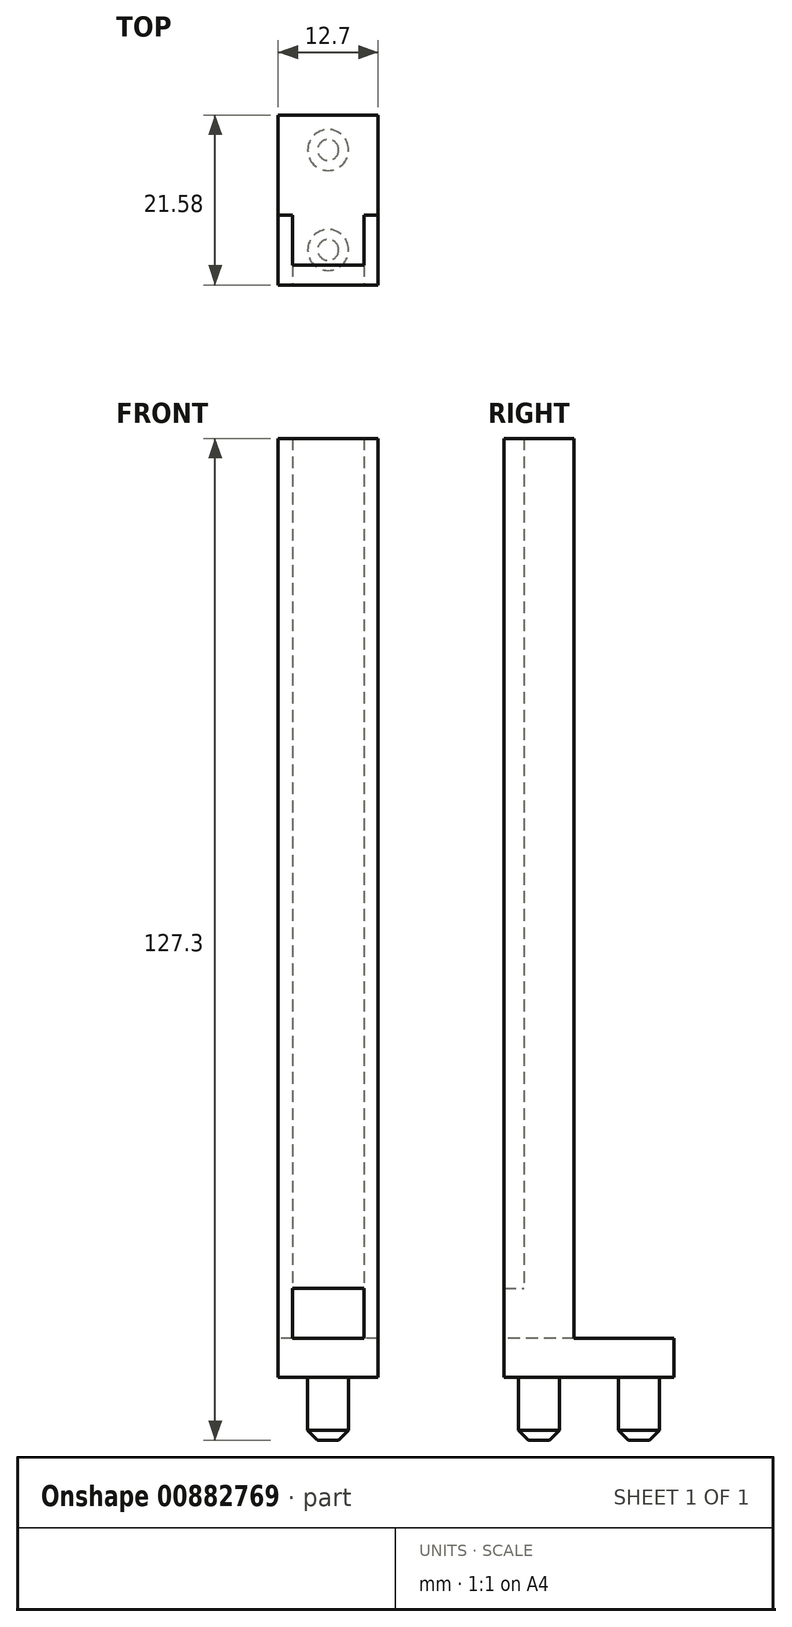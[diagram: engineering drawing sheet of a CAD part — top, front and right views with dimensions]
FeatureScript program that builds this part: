
annotation { "Feature Type Name" : "Feature", "Feature Type Description" : "" }
export const myFeature = defineFeature(function(context is Context, id is Id, definition is map)
    precondition{}
    {
        {
            var Q0;
            Q0=qCreatedBy(makeId("Top.planeOp"),FACE);
            var sketch = newSketch(context, id + "F0", { "sketchPlane" : qUnion([Q0])});
            skLineSegment(sketch, "E0.bottom", {"start": v(6.35, -10.8) * mm, "end": v(-6.35, -10.8) * mm});
            skLineSegment(sketch, "E0.top", {"start": v(6.35, 10.8) * mm, "end": v(-6.35, 10.8) * mm});
            skLineSegment(sketch, "E0.left", {"start": v(6.35, -10.8) * mm, "end": v(6.35, 10.8) * mm});
            skLineSegment(sketch, "E0.right", {"start": v(-6.35, -10.8) * mm, "end": v(-6.35, 10.8) * mm});
            skPoint(sketch, "E0.middle", {"position": v(0, 0) * mm});
            skSolve(sketch);
        }
        {
            var Q0;
            Q0 = qSketchRegion(id + "F0", true);
            extrude(context, id + "F1", {"entities" : qUnion([Q0]), "depth" : 5 * mm, "offsetDistance" : 25.4 * mm});
        }
        {
            var Q0;
            Q0=makeQuery(id+"F1.opExtrude","CAP_FACE",FACE,{"disambiguationData":[OSD([sQuery(id+"F0.wireOp",EDGE,"E0.bottom"),sQuery(id+"F0.wireOp",EDGE,"E0.top"),sQuery(id+"F0.wireOp",EDGE,"E0.left"),sQuery(id+"F0.wireOp",EDGE,"E0.right")])],"isStart":true});
            var sketch = newSketch(context, id + "F2", { "sketchPlane" : qUnion([Q0])});
            skCircle(sketch, "E1", {"center": v(0, 6.35) * mm, "radius": 2.6 * mm});
            skCircle(sketch, "E2", {"center": v(0, -6.35) * mm, "radius": 2.6 * mm});
            skSolve(sketch);
        }
        {
            var Q0;
            Q0 = qSketchRegion(id + "F2", true);
            extrude(context, id + "F3", {"entities" : qUnion([Q0]), "operationType" : NewBodyOperationType.ADD, "depth" : 8 * mm, "offsetDistance" : 25.4 * mm});
        }
        {
            var Q0;
            Q0=makeQuery(id+"F3.opExtrude","CAP_FACE",FACE,{"disambiguationData":[OSD([sQuery(id+"F2.wireOp",EDGE,"E1")])],"isStart":false});
            var Q1;
            Q1=makeQuery(id+"F3.opExtrude","CAP_FACE",FACE,{"disambiguationData":[OSD([sQuery(id+"F2.wireOp",EDGE,"E2")])],"isStart":false});
            chamfer(context, id + "F4", {"entities" : qUnion([Q0, Q1]), "width" : 1.27 * mm, "tangentPropagation" : true});
        }
        {
            var Q0;
            Q0=makeQuery(id+"F1.opExtrude","CAP_FACE",FACE,{"disambiguationData":[OSD([sQuery(id+"F0.wireOp",EDGE,"E0.bottom"),sQuery(id+"F0.wireOp",EDGE,"E0.top"),sQuery(id+"F0.wireOp",EDGE,"E0.left"),sQuery(id+"F0.wireOp",EDGE,"E0.right")])],"isStart":false});
            var sketch = newSketch(context, id + "F5", { "sketchPlane" : qUnion([Q0])});
            skLineSegment(sketch, "E3.bottom", {"start": v(6.35, -10.8) * mm, "end": v(-6.35, -10.8) * mm});
            skLineSegment(sketch, "E3.top", {"start": v(6.35, -1.9) * mm, "end": v(4.52, -1.9) * mm});
            skLineSegment(sketch, "E3.left", {"start": v(6.35, -10.8) * mm, "end": v(6.35, -1.9) * mm});
            skLineSegment(sketch, "E3.right", {"start": v(-6.35, -10.8) * mm, "end": v(-6.35, -1.9) * mm});
            skLineSegment(sketch, "E4.top", {"start": v(4.52, -8.26) * mm, "end": v(-4.52, -8.26) * mm});
            skLineSegment(sketch, "E4.left", {"start": v(4.52, -1.9) * mm, "end": v(4.52, -8.26) * mm});
            skLineSegment(sketch, "E4.right", {"start": v(-4.52, -1.9) * mm, "end": v(-4.52, -8.26) * mm});
            skLineSegment(sketch, "E5.trimOffspring", {"start": v(-4.52, -1.9) * mm, "end": v(-6.35, -1.9) * mm});
            skSolve(sketch);
        }
        {
            var Q0;
            Q0 = qSketchRegion(id + "F5", true);
            extrude(context, id + "F6", {"entities" : qUnion([Q0]), "operationType" : NewBodyOperationType.ADD, "depth" : 114.3 * mm, "offsetDistance" : 25.4 * mm});
        }
        {
            var Q0;
            Q0=makeQuery(id+"F6.opExtrude","SWEPT_FACE",FACE,{"disambiguationData":[OSD([sQuery(id+"F5.wireOp",EDGE,"E4.top")])]});
            var sketch = newSketch(context, id + "F7", { "sketchPlane" : qUnion([Q0])});
            skLineSegment(sketch, "E6.bottom", {"start": v(-4.52, 5) * mm, "end": v(4.52, 5) * mm});
            skLineSegment(sketch, "E6.top", {"start": v(-4.52, 11.35) * mm, "end": v(4.52, 11.35) * mm});
            skLineSegment(sketch, "E6.left", {"start": v(-4.52, 5) * mm, "end": v(-4.52, 11.35) * mm});
            skLineSegment(sketch, "E6.right", {"start": v(4.52, 5) * mm, "end": v(4.52, 11.35) * mm});
            skSolve(sketch);
        }
        {
            var Q0;
            Q0 = qSketchRegion(id + "F7", true);
            extrude(context, id + "F8", {"entities" : qUnion([Q0]), "operationType" : NewBodyOperationType.REMOVE, "endBound" : BoundingType.UP_TO_NEXT, "oppositeDirection" : true, "depth" : 25.4 * mm, "offsetDistance" : 25.4 * mm});
        }
    });
